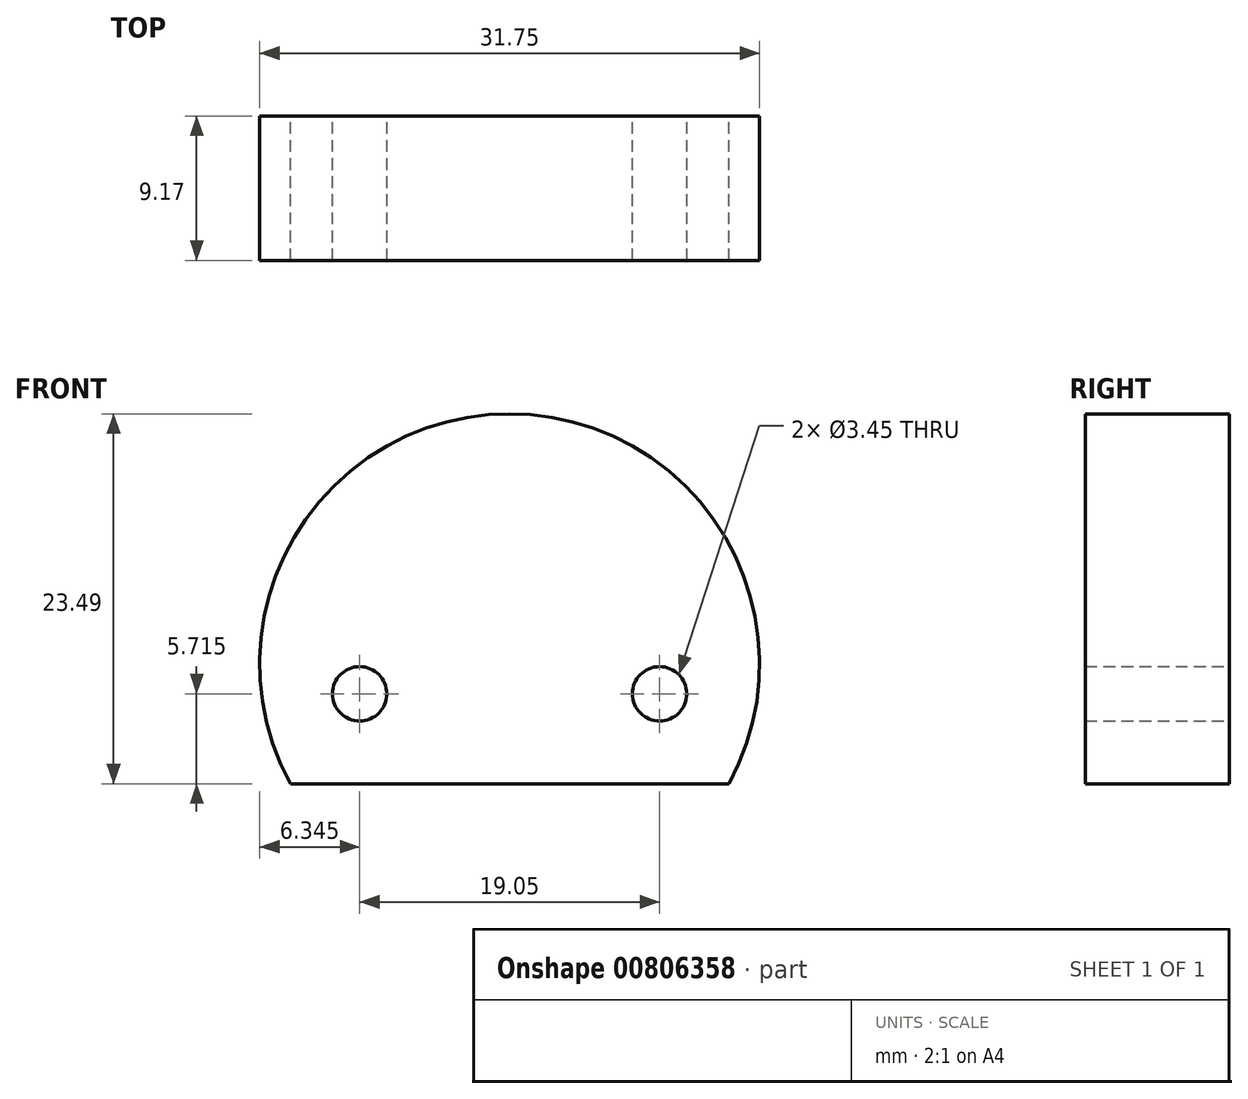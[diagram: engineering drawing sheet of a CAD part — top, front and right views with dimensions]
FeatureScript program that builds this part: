
annotation { "Feature Type Name" : "Feature", "Feature Type Description" : "" }
export const myFeature = defineFeature(function(context is Context, id is Id, definition is map)
    precondition{}
    {
        {
            var Q0;
            Q0=qCreatedBy(makeId("Front.planeOp"),FACE);
            var sketch = newSketch(context, id + "F0", { "sketchPlane" : qUnion([Q0])});
            skArc(sketch, "E0", {"start": v(13.93, -7.62) * mm, "mid": v(0, 15.88) * mm, "end": v(-13.93, -7.62) * mm});
            skLineSegment(sketch, "E1", {"start": v(-13.93, -7.62) * mm, "end": v(13.93, -7.62) * mm});
            skLineSegment(sketch, "E2", {"start": v(-12.6, -1.9) * mm, "end": v(11.15, -1.9) * mm, "construction": true});
            skCircle(sketch, "E3", {"center": v(-9.53, -1.9) * mm, "radius": 1.73 * mm});
            skCircle(sketch, "E4", {"center": v(9.53, -1.9) * mm, "radius": 1.73 * mm});
            skSolve(sketch);
        }
        {
            var Q0;
            Q0 = qSketchRegion(id + "F0", true);
            extrude(context, id + "F1", {"entities" : qUnion([Q0]), "depth" : 9.17 * mm, "offsetDistance" : 25.4 * mm});
        }
    });
